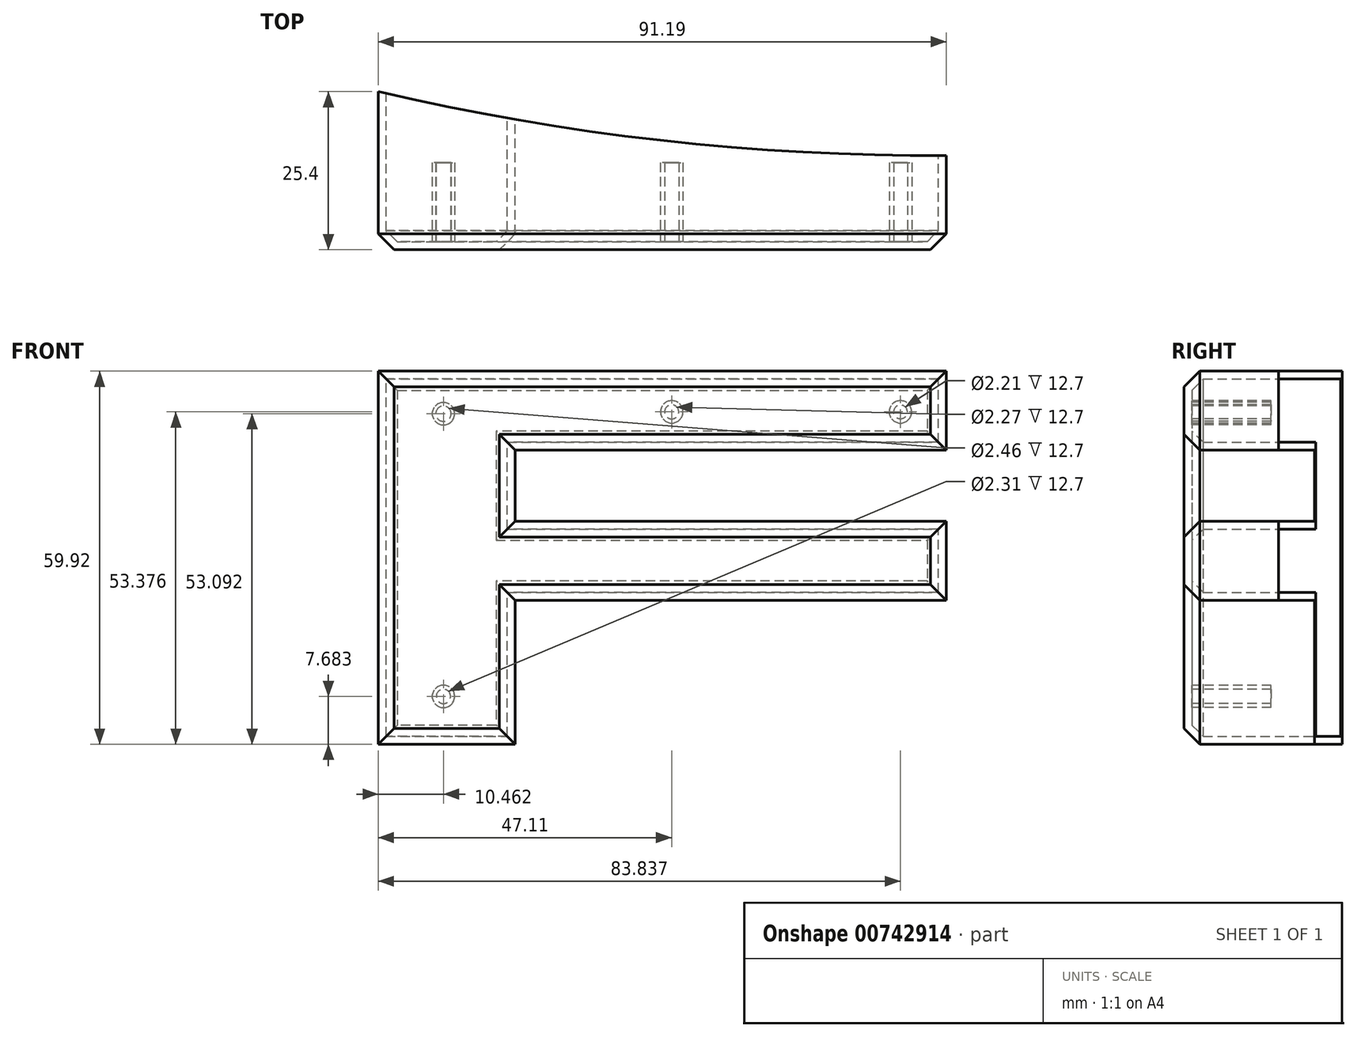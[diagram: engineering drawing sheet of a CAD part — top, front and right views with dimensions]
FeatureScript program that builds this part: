
annotation { "Feature Type Name" : "Feature", "Feature Type Description" : "" }
export const myFeature = defineFeature(function(context is Context, id is Id, definition is map)
    precondition{}
    {
        {
            var Q0;
            Q0=qCreatedBy(makeId("Front.planeOp"),FACE);
            var sketch = newSketch(context, id + "F0", { "sketchPlane" : qUnion([Q0])});
            skLineSegment(sketch, "E0", {"start": v(-47.11, 31.95) * mm, "end": v(-47.11, -27.97) * mm});
            skLineSegment(sketch, "E1", {"start": v(-47.11, 31.95) * mm, "end": v(44.08, 31.95) * mm});
            skLineSegment(sketch, "E2", {"start": v(44.08, 31.95) * mm, "end": v(44.08, 19.24) * mm});
            skLineSegment(sketch, "E3", {"start": v(44.08, 19.24) * mm, "end": v(-25.12, 19.24) * mm});
            skLineSegment(sketch, "E4", {"start": v(-25.12, 19.24) * mm, "end": v(-25.12, 7.87) * mm});
            skLineSegment(sketch, "E5", {"start": v(-25.12, 7.87) * mm, "end": v(44.08, 7.87) * mm});
            skLineSegment(sketch, "E6", {"start": v(44.08, 7.87) * mm, "end": v(44.08, -4.83) * mm});
            skLineSegment(sketch, "E7", {"start": v(44.08, -4.83) * mm, "end": v(-25.12, -4.83) * mm});
            skLineSegment(sketch, "E8", {"start": v(-25.12, -4.83) * mm, "end": v(-25.12, -27.97) * mm});
            skLineSegment(sketch, "E9", {"start": v(-25.12, -27.97) * mm, "end": v(-47.11, -27.97) * mm});
            skSolve(sketch);
        }
        {
            var Q0;
            Q0=makeQuery(id+"F0.imprint","IMPRINT",FACE,{"disambiguationData":[TD([[makeQuery(id+"F0.imprint","IMPRINT",EDGE,{"derivedFrom":sQuery(id+"F0.wireOp",EDGE,"E0")}),1.0]])]});
            extrude(context, id + "F1", {"entities" : qUnion([Q0]), "depth" : 25.4 * mm, "offsetDistance" : 25.4 * mm});
        }
        {
            var Q0;
            Q0=makeQuery(id+"F1.opExtrude","CAP_EDGE",EDGE,{"disambiguationData":[OSD([sQuery(id+"F0.wireOp",EDGE,"E1")])],"isStart":false});
            chamfer(context, id + "F2", {"entities" : qUnion([Q0]), "width" : 2.54 * mm, "tangentPropagation" : true});
        }
        {
            var Q0;
            Q0=makeQuery(id+"F1.opExtrude","CAP_EDGE",EDGE,{"disambiguationData":[OSD([sQuery(id+"F0.wireOp",EDGE,"E2")])],"isStart":false});
            var Q1;
            Q1=makeQuery(id+"F1.opExtrude","CAP_EDGE",EDGE,{"disambiguationData":[OSD([sQuery(id+"F0.wireOp",EDGE,"E3")])],"isStart":false});
            var Q2;
            Q2=makeQuery(id+"F1.opExtrude","CAP_EDGE",EDGE,{"disambiguationData":[OSD([sQuery(id+"F0.wireOp",EDGE,"E4")])],"isStart":false});
            var Q3;
            Q3=makeQuery(id+"F1.opExtrude","CAP_EDGE",EDGE,{"disambiguationData":[OSD([sQuery(id+"F0.wireOp",EDGE,"E5")])],"isStart":false});
            var Q4;
            Q4=makeQuery(id+"F1.opExtrude","CAP_EDGE",EDGE,{"disambiguationData":[OSD([sQuery(id+"F0.wireOp",EDGE,"E6")])],"isStart":false});
            var Q5;
            Q5=makeQuery(id+"F1.opExtrude","CAP_EDGE",EDGE,{"disambiguationData":[OSD([sQuery(id+"F0.wireOp",EDGE,"E7")])],"isStart":false});
            var Q6;
            Q6=makeQuery(id+"F1.opExtrude","CAP_EDGE",EDGE,{"disambiguationData":[OSD([sQuery(id+"F0.wireOp",EDGE,"E8")])],"isStart":false});
            var Q7;
            Q7=makeQuery(id+"F1.opExtrude","CAP_EDGE",EDGE,{"disambiguationData":[OSD([sQuery(id+"F0.wireOp",EDGE,"E9")])],"isStart":false});
            var Q8;
            Q8=makeQuery(id+"F1.opExtrude","CAP_EDGE",EDGE,{"disambiguationData":[OSD([sQuery(id+"F0.wireOp",EDGE,"E0")])],"isStart":false});
            chamfer(context, id + "F3", {"entities" : qUnion([Q0, Q1, Q2, Q3, Q4, Q5, Q6, Q7, Q8]), "width" : 2.54 * mm, "tangentPropagation" : true});
        }
        {
            var Q0;
            Q0=makeQuery(id+"F1.opExtrude","CAP_FACE",FACE,{"disambiguationData":[OSD([sQuery(id+"F0.wireOp",EDGE,"E0"),sQuery(id+"F0.wireOp",EDGE,"E1"),sQuery(id+"F0.wireOp",EDGE,"E2"),sQuery(id+"F0.wireOp",EDGE,"E3"),sQuery(id+"F0.wireOp",EDGE,"E4"),sQuery(id+"F0.wireOp",EDGE,"E5"),sQuery(id+"F0.wireOp",EDGE,"E6"),sQuery(id+"F0.wireOp",EDGE,"E7"),sQuery(id+"F0.wireOp",EDGE,"E8"),sQuery(id+"F0.wireOp",EDGE,"E9")])],"isStart":true});
            shell(context, id + "F4", {"entities" : qUnion([Q0]), "thickness" : 1.27 * mm});
        }
        {
            var Q0;
            Q0=makeQuery(id+"F1.opExtrude","SWEPT_FACE",FACE,{"disambiguationData":[OSD([sQuery(id+"F0.wireOp",EDGE,"E7")])]});
            var sketch = newSketch(context, id + "F5", { "sketchPlane" : qUnion([Q0])});
            skArc(sketch, "E10", {"start": v(44.08, 10.26) * mm, "mid": v(-1.82, 7.83) * mm, "end": v(-47.11, 0) * mm});
            skLineSegment(sketch, "E11", {"start": v(-47.11, 0) * mm, "end": v(44.08, 0) * mm});
            skLineSegment(sketch, "E12", {"start": v(44.08, 0) * mm, "end": v(44.08, 10.26) * mm});
            skSolve(sketch);
        }
        {
            var Q0;
            Q0 = qSketchRegion(id + "F5", true);
            extrude(context, id + "F6", {"entities" : qUnion([Q0]), "operationType" : NewBodyOperationType.REMOVE, "endBound" : BoundingType.SYMMETRIC, "depth" : 76.2 * mm, "offsetDistance" : 25.4 * mm});
        }
        {
            var Q0;
            Q0=makeQuery(id+"F4.opShell","OFFSET_FACE",FACE,{"disambiguationData":[OSD([sQuery(id+"F0.wireOp",EDGE,"E0"),sQuery(id+"F0.wireOp",EDGE,"E1"),sQuery(id+"F0.wireOp",EDGE,"E2"),sQuery(id+"F0.wireOp",EDGE,"E3"),sQuery(id+"F0.wireOp",EDGE,"E4"),sQuery(id+"F0.wireOp",EDGE,"E5"),sQuery(id+"F0.wireOp",EDGE,"E6"),sQuery(id+"F0.wireOp",EDGE,"E7"),sQuery(id+"F0.wireOp",EDGE,"E8"),sQuery(id+"F0.wireOp",EDGE,"E9")])]});
            var sketch = newSketch(context, id + "F7", { "sketchPlane" : qUnion([Q0])});
            skCircle(sketch, "E13", {"center": v(-36.73, 25.4) * mm, "radius": 1.8 * mm});
            skCircle(sketch, "E14", {"center": v(0, 25.4) * mm, "radius": 1.8 * mm});
            skCircle(sketch, "E15", {"center": v(36.65, 25.12) * mm, "radius": 1.8 * mm});
            skCircle(sketch, "E16", {"center": v(36.65, -20.29) * mm, "radius": 1.8 * mm});
            skCircle(sketch, "E17", {"center": v(-36.73, 25.4) * mm, "radius": 1.1 * mm});
            skCircle(sketch, "E18", {"center": v(0, 25.4) * mm, "radius": 1.14 * mm});
            skCircle(sketch, "E19", {"center": v(36.65, 25.12) * mm, "radius": 1.23 * mm});
            skCircle(sketch, "E20", {"center": v(36.65, -20.29) * mm, "radius": 1.15 * mm});
            skSolve(sketch);
        }
        {
            var Q0;
            Q0 = qSketchRegion(id + "F7", true);
            extrude(context, id + "F8", {"entities" : qUnion([Q0]), "operationType" : NewBodyOperationType.ADD, "depth" : 12.7 * mm, "offsetDistance" : 25.4 * mm});
        }
    });
